FCSTD DOCUMENT  (FreeCAD 0.19R)
Label: fc_assy
License: All rights reserved
LicenseURL: http://en.wikipedia.org/wiki/All_rights_reserved
objects: App::DocumentObjectGroup×2, App::Link×2, PartDesign::CoordinateSystem×1, App::FeaturePython×1, App::Part×1
note: 1 computed .brp shape members not serialized (recipe doc carries the construction recipe); baked Part::Feature solids carry a one-line shape summary decoded from their .brp
EXTERNAL_REF file=fc_box.FCStd obj=LCS_1
EXTERNAL_REF file=fc_box.FCStd obj=Body
EXTERNAL_REF file=cover.FCStd obj=LCS_1
EXTERNAL_REF file=fc_box.FCStd obj=LCS_2
EXTERNAL_REF file=cover.FCStd obj=Body

FEATURE [App::DocumentObjectGroup] Parts
FEATURE [PartDesign::CoordinateSystem] LCS_Origin
  AttacherType = Attacher::AttachEngine3D
  MapMode = 2
  Support = -> [X_Axis]
FEATURE [App::DocumentObjectGroup] Constraints
FEATURE [App::FeaturePython] Variables  # WARN: FeaturePython — macro-defined, semantics opaque (R4)
FEATURE [App::Link] fc_box_Body
  AssemblyType = Asm4EE
  AttachedBy = #LCS_1
  AttachedTo = Parent Assembly#LCS_Origin
  LinkPlacement = pos=(-21,-21,0) rot=(0,0,1;0rad)
  LinkedObject = -> <external fc_box.FCStd>#Body
  Placement = pos=(-21,-21,0) rot=(0,0,1;0rad)
  expr: Placement = LCS_Origin.Placement * AttachmentOffset * fc_box#LCS_1.Placement ^ -1
FEATURE [App::Link] cover_Body
  AssemblyType = Asm4EE
  AttachedBy = #LCS_1
  AttachedTo = fc_box_Body#LCS_2
  AttachmentOffset = pos=(0,0,0) rot=(0,1,0;3.14159rad)
  LinkPlacement = pos=(-21,-92.5,24) rot=(0,0,1;0rad)
  LinkedObject = -> <external cover.FCStd>#Body
  Placement = pos=(-21,-92.5,24) rot=(0,0,1;0rad)
  expr: Placement = fc_box_Body.Placement * fc_box#LCS_2.Placement * AttachmentOffset * cover#LCS_1.Placement ^ -1
FEATURE [App::Part] Model
  Configuration = 0
  Group = -> [LCS_Origin,Constraints,Variables,fc_box_Body,cover_Body]
  Origin = -> Origin
  Type = Assembly4 Model

RESOLVED EXTERNAL PARTS (link-assembly join: the EXTERNAL_REF files above that resolve inside this repo's crawl, each included once):
---- part cover.FCStd = doc fcstd_2b1ffa46e12e ----
FCSTD DOCUMENT  (FreeCAD 0.19R)
Label: cover
License: All rights reserved
LicenseURL: http://en.wikipedia.org/wiki/All_rights_reserved
objects: Sketcher::SketchObject×10, PartDesign::Pad×5, PartDesign::Pocket×5, PartDesign::Chamfer×5, PartDesign::CoordinateSystem×1, PartDesign::Body×1
note: 42 computed .brp shape members not serialized (recipe doc carries the construction recipe); baked Part::Feature solids carry a one-line shape summary decoded from their .brp

FEATURE [Sketcher::SketchObject] Sketch
  FullyConstrained = true
  MapMode = 5
  Support = -> [XY_Plane]
  sketch-geometry (8):
    g0: LineSegment StartX=-23.5 StartY=95 StartZ=0 EndX=23.5 EndY=95 EndZ=0
    g1: LineSegment StartX=23.5 StartY=95 StartZ=0 EndX=23.5 EndY=48 EndZ=0
    g2: LineSegment StartX=23.5 StartY=48 StartZ=0 EndX=20.5 EndY=48 EndZ=0
    g3: LineSegment StartX=20.5 StartY=48 StartZ=0 EndX=20.5 EndY=0 EndZ=0
    g4: LineSegment StartX=20.5 StartY=0 StartZ=0 EndX=-20.5 EndY=0 EndZ=0
    g5: LineSegment StartX=-20.5 StartY=0 StartZ=0 EndX=-20.5 EndY=48 EndZ=0
    g6: LineSegment StartX=-20.5 StartY=48 StartZ=0 EndX=-23.5 EndY=48 EndZ=0
    g7: LineSegment StartX=-23.5 StartY=48 StartZ=0 EndX=-23.5 EndY=95 EndZ=0
  constraints (22):
    c: Coincident(g0,g1)
    c: Vertical(g1)
    c: Coincident(g1,g2)
    c: Horizontal(g2)
    c: Coincident(g2,g3)
    c: Vertical(g3)
    c: Coincident(g3,g4)
    c: Coincident(g4,g5)
    c: Vertical(g5)
    c: Coincident(g5,g6)
    c: Horizontal(g6)
    c: Coincident(g6,g7)
    c: Coincident(g7,g0)
    c: Vertical(g7)
    c: DistanceX(g0,g0) = 47
    c: Symmetric(g0,g0,g-2)
    c: DistanceY(g1,g1) = 47
    c: Equal(g7,g1)
    c: DistanceX(g4,g4) = 41
    c: Symmetric(g4,g3,g-2)
    c: PointOnObject(g3,g-1)
    c: DistanceY(g3,g3) = 48
FEATURE [PartDesign::Pad] Pad
  Direction = (1,1,1)
  Length = 7
  Length2 = 100
  Profile = -> Sketch
  Type = 0
FEATURE [Sketcher::SketchObject] Sketch001
  ExternalGeometry = -> [Pad]
  FullyConstrained = true
  MapMode = 5
  Placement = pos=(0,0,0) rot=(1,0,0;3.14159rad)
  Support = -> [Pad]
  sketch-geometry (8):
    g0: LineSegment StartX=-18.5 StartY=-2 StartZ=0 EndX=18.5 EndY=-2 EndZ=0
    g1: LineSegment StartX=18.5 StartY=-2 StartZ=0 EndX=18.5 EndY=-50 EndZ=0
    g2: LineSegment StartX=18.5 StartY=-50 StartZ=0 EndX=21.5 EndY=-50 EndZ=0
    g3: LineSegment StartX=21.5 StartY=-50 StartZ=0 EndX=21.5 EndY=-93 EndZ=0
    g4: LineSegment StartX=21.5 StartY=-93 StartZ=0 EndX=-21.5 EndY=-93 EndZ=0
    g5: LineSegment StartX=-21.5 StartY=-93 StartZ=0 EndX=-21.5 EndY=-50 EndZ=0
    g6: LineSegment StartX=-21.5 StartY=-50 StartZ=0 EndX=-18.5 EndY=-50 EndZ=0
    g7: LineSegment StartX=-18.5 StartY=-50 StartZ=0 EndX=-18.5 EndY=-2 EndZ=0
  constraints (24):
    c: Horizontal(g0)
    c: Coincident(g0,g1)
    c: Vertical(g1)
    c: Coincident(g1,g2)
    c: Horizontal(g2)
    c: Coincident(g2,g3)
    c: Vertical(g3)
    c: Coincident(g3,g4)
    c: Horizontal(g4)
    c: Coincident(g4,g5)
    c: Vertical(g5)
    c: Coincident(g5,g6)
    c: Horizontal(g6)
    c: Coincident(g6,g7)
    c: Coincident(g7,g0)
    c: Vertical(g7)
    c: DistanceY(g-6,g4) = 2
    c: DistanceX(g-6,g5) = 2
    c: DistanceY(g5,g-6) = 2
    c: DistanceX(g-3,g0) = 2
    c: DistanceX(g0,g-4) = 2
    c: DistanceY(g0,g-3) = 2
    c: DistanceY(g2,g-5) = 2
    c: DistanceX(g3,g-5) = 2
FEATURE [PartDesign::Pocket] Pocket
  BaseFeature = -> Pad
  Length = 5
  Length2 = 100
  Profile = -> Sketch001
  Type = 0
FEATURE [PartDesign::CoordinateSystem] LCS_1
  AttacherType = Attacher::AttachEngine3D
  AttachmentOffset = pos=(0,0,-21.5) rot=(0,0,1;0rad)
  MapMode = 7
  Placement = pos=(0,93,5) rot=(0.57735,0.57735,0.57735;2.0944rad)
  Support = -> [Pocket]
FEATURE [Sketcher::SketchObject] Sketch002
  ExternalGeometry = -> [Pocket]
  FullyConstrained = true
  MapMode = 5
  Placement = pos=(0,0,7) rot=(0,0,1;0rad)
  Support = -> [Pocket]
  sketch-geometry (8):
    g0: LineSegment StartX=-16 StartY=46 StartZ=0 EndX=16 EndY=46 EndZ=0
    g1: LineSegment StartX=16 StartY=46 StartZ=0 EndX=16 EndY=43 EndZ=0
    g2: LineSegment StartX=16 StartY=43 StartZ=0 EndX=-16 EndY=43 EndZ=0
    g3: LineSegment StartX=-16 StartY=43 StartZ=0 EndX=-16 EndY=46 EndZ=0
    g4: LineSegment StartX=-16 StartY=37 StartZ=0 EndX=16 EndY=37 EndZ=0
    g5: LineSegment StartX=16 StartY=37 StartZ=0 EndX=16 EndY=34 EndZ=0
    g6: LineSegment StartX=16 StartY=34 StartZ=0 EndX=-16 EndY=34 EndZ=0
    g7: LineSegment StartX=-16 StartY=34 StartZ=0 EndX=-16 EndY=37 EndZ=0
  constraints (22):
    c: Coincident(g0,g1)
    c: Coincident(g1,g2)
    c: Coincident(g2,g3)
    c: Coincident(g3,g0)
    c: Horizontal(g0)
    c: Vertical(g1)
    c: Vertical(g3)
    c: Coincident(g4,g5)
    c: Coincident(g5,g6)
    c: Coincident(g6,g7)
    c: Coincident(g7,g4)
    c: Horizontal(g6)
    c: Vertical(g5)
    c: Vertical(g7)
    c: Equal(g5,g1)
    c: Symmetric(g1,g2,g-2)
    c: DistanceY(g1,g-3) = 5
    c: Equal(g4,g2)
    c: Symmetric(g4,g4,g-2)
    c: DistanceY(g4,g1) = 6
    c: DistanceY(g5,g4) = 3
    c: DistanceX(g4,g4) = 32
FEATURE [PartDesign::Pad] Pad001
  BaseFeature = -> Pocket
  Direction = (1,1,1)
  Length = 5
  Length2 = 100
  Profile = -> Sketch002
  Type = 0
FEATURE [Sketcher::SketchObject] Sketch003
  ExternalGeometry = -> [Pad001]
  FullyConstrained = true
  MapMode = 5
  Placement = pos=(0,0,7) rot=(0,0,1;0rad)
  Support = -> [Pad001]
  sketch-geometry (4):
    g0: LineSegment StartX=-20.5 StartY=87 StartZ=0 EndX=-10.5 EndY=87 EndZ=0
    g1: LineSegment StartX=-10.5 StartY=87 StartZ=0 EndX=-10.5 EndY=75 EndZ=0
    g2: LineSegment StartX=-10.5 StartY=75 StartZ=0 EndX=-20.5 EndY=75 EndZ=0
    g3: LineSegment StartX=-20.5 StartY=75 StartZ=0 EndX=-20.5 EndY=87 EndZ=0
  constraints (12):
    c: Coincident(g0,g1)
    c: Coincident(g1,g2)
    c: Coincident(g2,g3)
    c: Coincident(g3,g0)
    c: Horizontal(g0)
    c: Horizontal(g2)
    c: Vertical(g1)
    c: Vertical(g3)
    c: DistanceX(g0,g0) = 10
    c: DistanceY(g1,g1) = 12
    c: DistanceY(g0,g-3) = 8
    c: DistanceX(g-3,g0) = 3
FEATURE [PartDesign::Pocket] Pocket001
  BaseFeature = -> Pad001
  Length = 2
  Length2 = 100
  Profile = -> Sketch003
  Type = 0
FEATURE [Sketcher::SketchObject] Sketch004
  ExternalGeometry = -> [Pocket001]
  FullyConstrained = true
  MapMode = 5
  Placement = pos=(0,0,7) rot=(0,0,1;0rad)
  Support = -> [Pocket001]
  sketch-geometry (8):
    g0: LineSegment StartX=-9.5 StartY=95 StartZ=0 EndX=15.5 EndY=95 EndZ=0
    g1: LineSegment StartX=-9.5 StartY=95 StartZ=0 EndX=-9.5 EndY=73 EndZ=0
    g2: LineSegment StartX=15.5 StartY=73 StartZ=0 EndX=15.5 EndY=95 EndZ=0
    g3: LineSegment StartX=-9.5 StartY=73 StartZ=0 EndX=-7.5 EndY=73 EndZ=0
    g4: LineSegment StartX=15.5 StartY=73 StartZ=0 EndX=13.5 EndY=73 EndZ=0
    g5: LineSegment StartX=-7.5 StartY=73 StartZ=0 EndX=-7.5 EndY=88 EndZ=0
    g6: LineSegment StartX=-7.5 StartY=88 StartZ=0 EndX=13.5 EndY=88 EndZ=0
    g7: LineSegment StartX=13.5 StartY=88 StartZ=0 EndX=13.5 EndY=73 EndZ=0
  constraints (24):
    c: PointOnObject(g0,g-3)
    c: PointOnObject(g0,g-3)
    c: DistanceX(g0,g0) = 25
    c: DistanceX(g-3,g0) = 14
    c: Coincident(g0,g1)
    c: Vertical(g1)
    c: Coincident(g2,g0)
    c: Vertical(g2)
    c: Coincident(g3,g1)
    c: Horizontal(g3)
    c: Coincident(g4,g2)
    c: Horizontal(g4)
    c: Equal(g4,g3)
    c: DistanceX(g4,g4) = 2
    c: Equal(g2,g1)
    c: DistanceY(g2,g2) = 22
    c: Coincident(g3,g5)
    c: Vertical(g5)
    c: Coincident(g5,g6)
    c: Horizontal(g6)
    c: Coincident(g6,g7)
    c: Coincident(g7,g4)
    c: Vertical(g7)
    c: DistanceY(g6,g0) = 7
FEATURE [PartDesign::Pad] Pad002
  BaseFeature = -> Pocket001
  Direction = (1,1,1)
  Length = 20
  Length2 = 100
  Profile = -> Sketch004
  Type = 0
FEATURE [Sketcher::SketchObject] Sketch005
  ExternalGeometry = -> [Pad002]
  FullyConstrained = true
  MapMode = 5
  Placement = pos=(-7.5,0,0) rot=(0.57735,0.57735,0.57735;2.0944rad)
  Support = -> [Pad002]
  sketch-geometry (2):
    g0: ArcOfCircle CenterX=81 CenterY=7 CenterZ=0 NormalX=0 NormalY=0 NormalZ=1 AngleXU=0 Radius=6 StartAngle=1.42e-14 EndAngle=3.14159
    g1: LineSegment StartX=75 StartY=7 StartZ=0 EndX=87 EndY=7 EndZ=0
  constraints (5):
    c: PointOnObject(g0,g-3)
    c: Coincident(g0,g-4)
    c: Coincident(g0,g-5)
    c: Coincident(g1,g0)
    c: Coincident(g1,g0)
FEATURE [PartDesign::Pocket] Pocket002
  BaseFeature = -> Pad002
  Length = 5
  Length2 = 100
  Profile = -> Sketch005
  Type = 0
FEATURE [Sketcher::SketchObject] Sketch006
  ExternalGeometry = -> [Pad002]
  FullyConstrained = true
  MapMode = 5
  Placement = pos=(-5.42e-14,95,0) rot=(0,0.707107,0.707107;3.14159rad)
  Support = -> [Pad002]
  sketch-geometry (1):
    g0: Circle CenterX=-3 CenterY=18 CenterZ=0 NormalX=0 NormalY=0 NormalZ=1 AngleXU=0 Radius=5
  constraints (3):
    c: Diameter(g0) = 10
    c: DistanceY(g0,g-3) = 9
    c: DistanceX(g-3,g0) = 12.5
FEATURE [PartDesign::Pocket] Pocket003
  BaseFeature = -> Pocket002
  Length = 7
  Length2 = 100
  Profile = -> Sketch006
  Type = 0
FEATURE [Sketcher::SketchObject] Sketch007
  ExternalGeometry = -> [Pocket003]
  FullyConstrained = true
  MapMode = 5
  Placement = pos=(0,0,27) rot=(0,0,1;0rad)
  Support = -> [Pocket003]
  sketch-geometry (8):
    g0: LineSegment StartX=-9.5 StartY=73 StartZ=0 EndX=-0.5 EndY=73 EndZ=0
    g1: LineSegment StartX=-0.5 StartY=73 StartZ=0 EndX=-0.5 EndY=81 EndZ=0
    g2: LineSegment StartX=-0.5 StartY=81 StartZ=0 EndX=6.5 EndY=81 EndZ=0
    g3: LineSegment StartX=6.5 StartY=81 StartZ=0 EndX=6.5 EndY=73 EndZ=0
    g4: LineSegment StartX=6.5 StartY=73 StartZ=0 EndX=15.5 EndY=73 EndZ=0
    g5: LineSegment StartX=15.5 StartY=73 StartZ=0 EndX=15.5 EndY=95 EndZ=0
    g6: LineSegment StartX=15.5 StartY=95 StartZ=0 EndX=-9.5 EndY=95 EndZ=0
    g7: LineSegment StartX=-9.5 StartY=95 StartZ=0 EndX=-9.5 EndY=73 EndZ=0
  constraints (20):
    c: Coincident(g-3,g0)
    c: Horizontal(g0)
    c: Coincident(g0,g1)
    c: Vertical(g1)
    c: Coincident(g1,g2)
    c: Horizontal(g2)
    c: Coincident(g2,g3)
    c: Vertical(g3)
    c: Coincident(g3,g4)
    c: Coincident(g4,g-5)
    c: Coincident(g4,g5)
    c: Coincident(g5,g-5)
    c: Coincident(g5,g6)
    c: Coincident(g6,g-4)
    c: Coincident(g6,g7)
    c: Coincident(g7,g0)
    c: Horizontal(g4)
    c: Equal(g0,g4)
    c: DistanceY(g2,g-6) = 7
    c: DistanceX(g2,g2) = 7
FEATURE [PartDesign::Pad] Pad003
  BaseFeature = -> Pocket003
  Direction = (1,1,1)
  Length = 3
  Length2 = 100
  Profile = -> Sketch007
  Type = 0
FEATURE [Sketcher::SketchObject] Sketch008
  ExternalGeometry = -> [Pad003]
  FullyConstrained = true
  MapMode = 5
  Placement = pos=(0,0,30) rot=(0,0,1;0rad)
  Support = -> [Pad003]
  sketch-geometry (9):
    g0: LineSegment StartX=-0.5 StartY=73 StartZ=0 EndX=-0.5 EndY=81 EndZ=0
    g1: LineSegment StartX=-0.5 StartY=81 StartZ=0 EndX=6.5 EndY=81 EndZ=0
    g2: LineSegment StartX=6.5 StartY=81 StartZ=0 EndX=6.5 EndY=73 EndZ=0
    g3: LineSegment StartX=6.5 StartY=73 StartZ=0 EndX=9.5 EndY=73 EndZ=0
    g4: LineSegment StartX=9.5 StartY=73 StartZ=0 EndX=9.5 EndY=82 EndZ=0
    g5: LineSegment StartX=9.5 StartY=82 StartZ=0 EndX=2.5 EndY=95 EndZ=0
    g6: LineSegment StartX=2.5 StartY=95 StartZ=0 EndX=-3.5 EndY=82 EndZ=0
    g7: LineSegment StartX=-3.5 StartY=82 StartZ=0 EndX=-3.5 EndY=73 EndZ=0
    g8: LineSegment StartX=-3.5 StartY=73 StartZ=0 EndX=-0.5 EndY=73 EndZ=0
  constraints (23):
    c: Coincident(g-6,g0)
    c: Coincident(g0,g-6)
    c: Coincident(g0,g1)
    c: Coincident(g1,g-5)
    c: Coincident(g1,g2)
    c: Coincident(g2,g-5)
    c: Coincident(g2,g3)
    c: Horizontal(g3)
    c: Coincident(g3,g4)
    c: Vertical(g4)
    c: Coincident(g4,g5)
    c: PointOnObject(g5,g-3)
    c: Coincident(g5,g6)
    c: Coincident(g6,g7)
    c: Vertical(g7)
    c: Coincident(g7,g8)
    c: Coincident(g8,g0)
    c: Horizontal(g8)
    c: Equal(g7,g4)
    c: Equal(g8,g3)
    c: DistanceX(g3,g3) = 3
    c: DistanceY(g7,g7) = 9
    c: DistanceX(g5,g4) = 7
FEATURE [PartDesign::Pad] Pad004
  BaseFeature = -> Pad003
  Direction = (1,1,1)
  Length = 40
  Length2 = 100
  Profile = -> Sketch008
  Type = 0
FEATURE [PartDesign::Chamfer] Chamfer
  Angle = 45
  Base = -> Pad004 [Edge58]
  BaseFeature = -> Pad004
  ChamferType = 0
  FlipDirection = false
  Size = 5
  Size2 = 1
  SupportTransform = false
FEATURE [PartDesign::Chamfer] Chamfer001
  Angle = 45
  Base = -> Chamfer [Edge46]
  BaseFeature = -> Chamfer
  ChamferType = 0
  FlipDirection = false
  Size = 5
  Size2 = 1
  SupportTransform = false
FEATURE [PartDesign::Chamfer] Chamfer002
  Angle = 45
  Base = -> Chamfer001 [Edge176,Edge174]
  BaseFeature = -> Chamfer001
  ChamferType = 0
  FlipDirection = false
  Size = 3
  Size2 = 1
  SupportTransform = false
FEATURE [PartDesign::Chamfer] Chamfer003
  Angle = 45
  Base = -> Chamfer002 [Edge156]
  BaseFeature = -> Chamfer002
  ChamferType = 0
  FlipDirection = false
  Size = 1
  Size2 = 1
  SupportTransform = false
FEATURE [PartDesign::Chamfer] Chamfer004
  Angle = 45
  Base = -> Chamfer003 [Edge106]
  BaseFeature = -> Chamfer003
  ChamferType = 0
  FlipDirection = false
  Size = 1
  Size2 = 1
  SupportTransform = false
FEATURE [Sketcher::SketchObject] Sketch009
  ExternalGeometry = -> [Chamfer004]
  FullyConstrained = true
  MapMode = 5
  Placement = pos=(15.5,0,0) rot=(0.57735,0.57735,0.57735;2.0944rad)
  Support = -> [Chamfer004]
  sketch-geometry (1):
    g0: Circle CenterX=78 CenterY=19 CenterZ=0 NormalX=0 NormalY=0 NormalZ=1 AngleXU=0 Radius=2.5
  constraints (3):
    c: Diameter(g0) = 5
    c: DistanceX(g-3,g0) = 5
    c: DistanceY(g0,g-3) = 8
FEATURE [PartDesign::Pocket] Pocket004
  BaseFeature = -> Chamfer004
  Length = 5
  Length2 = 100
  Profile = -> Sketch009
  Type = 1
FEATURE [PartDesign::Body] Body
  Group = -> [Sketch,Pad,Sketch001,Pocket,LCS_1,Sketch002,Pad001,Sketch003,Pocket001,Sketch004,Pad002,Sketch005,Pocket002,Sketch006,Pocket003,Sketch007,Pad003,Sketch008,Pad004,Chamfer,Chamfer001,Chamfer002,Chamfer003,Chamfer004,Sketch009,Pocket004]
  Origin = -> Origin
  Tip = -> Pocket004
---- part fc_box.FCStd = doc fcstd_bd3612893a7e ----
FCSTD DOCUMENT  (FreeCAD 0.19R)
Label: fc_box
License: All rights reserved
LicenseURL: http://en.wikipedia.org/wiki/All_rights_reserved
objects: Sketcher::SketchObject×9, PartDesign::Pocket×5, PartDesign::Pad×4, PartDesign::CoordinateSystem×2, PartDesign::Body×1
note: 30 computed .brp shape members not serialized (recipe doc carries the construction recipe); baked Part::Feature solids carry a one-line shape summary decoded from their .brp

FEATURE [Sketcher::SketchObject] Sketch
  FullyConstrained = true
  MapMode = 5
  Support = -> [XY_Plane]
  sketch-geometry (12):
    g0: LineSegment StartX=-21 StartY=21 StartZ=0 EndX=21 EndY=21 EndZ=0
    g1: LineSegment StartX=21 StartY=21 StartZ=0 EndX=21 EndY=-21 EndZ=0
    g2: LineSegment StartX=-21 StartY=-21 StartZ=0 EndX=-21 EndY=21 EndZ=0
    g3: Circle CenterX=-15 CenterY=15 CenterZ=0 NormalX=0 NormalY=0 NormalZ=1 AngleXU=0 Radius=1.75
    g4: Circle CenterX=15 CenterY=15 CenterZ=0 NormalX=0 NormalY=0 NormalZ=1 AngleXU=0 Radius=1.75
    g5: Circle CenterX=-15 CenterY=-15 CenterZ=0 NormalX=0 NormalY=0 NormalZ=1 AngleXU=0 Radius=1.75
    g6: Circle CenterX=15 CenterY=-15 CenterZ=0 NormalX=0 NormalY=0 NormalZ=1 AngleXU=0 Radius=1.75
    g7: LineSegment StartX=-18 StartY=-69 StartZ=0 EndX=18 EndY=-69 EndZ=0
    g8: LineSegment StartX=-21 StartY=-21 StartZ=0 EndX=-18 EndY=-21 EndZ=0
    g9: LineSegment StartX=21 StartY=-21 StartZ=0 EndX=18 EndY=-21 EndZ=0
    g10: LineSegment StartX=-18 StartY=-69 StartZ=0 EndX=-18 EndY=-21 EndZ=0
    g11: LineSegment StartX=18 StartY=-69 StartZ=0 EndX=18 EndY=-21 EndZ=0
  constraints (31):
    c: Coincident(g0,g1)
    c: Coincident(g2,g0)
    c: Vertical(g2)
    c: Symmetric(g0,g0,g-2)
    c: Symmetric(g1,g0,g-1)
    c: DistanceX(g0,g0) = 42
    c: Equal(g3,g4)
    c: Equal(g4,g6)
    c: Equal(g6,g5)
    c: Diameter(g3) = 3.5
    c: DistanceX(g0,g3) = 6
    c: Symmetric(g3,g4,g-2)
    c: DistanceY(g3,g0) = 6
    c: Symmetric(g5,g6,g-2)
    c: DistanceX(g0,g5) = 6
    c: DistanceY(g5,g3) = 30
    c: DistanceY(g1,g1) = 42
    c: Equal(g2,g1)
    c: Symmetric(g7,g7,g-2)
    c: Coincident(g8,g2)
    c: Horizontal(g8)
    c: Coincident(g9,g1)
    c: Horizontal(g9)
    c: Equal(g8,g9)
    c: Coincident(g10,g7)
    c: Coincident(g10,g8)
    c: Vertical(g10)
    c: Coincident(g11,g7)
    c: Coincident(g11,g9)
    c: DistanceX(g7,g7) = 36
    c: DistanceY(g11,g11) = 48
FEATURE [PartDesign::Pad] Pad
  Direction = (1,1,1)
  Length = 4
  Length2 = 100
  Profile = -> Sketch
  Type = 0
FEATURE [Sketcher::SketchObject] Sketch001
  ExternalGeometry = -> [Pad]
  FullyConstrained = true
  MapMode = 5
  Placement = pos=(0,0,4) rot=(0,0,1;0rad)
  Support = -> [Pad]
  sketch-geometry (16):
    g0: LineSegment StartX=-19 StartY=19 StartZ=0 EndX=-19 EndY=-19 EndZ=0
    g1: LineSegment StartX=-19 StartY=-19 StartZ=0 EndX=-16 EndY=-19 EndZ=0
    g2: LineSegment StartX=-16 StartY=-19 StartZ=0 EndX=-16 EndY=-67 EndZ=0
    g3: LineSegment StartX=-16 StartY=-67 StartZ=0 EndX=16 EndY=-67 EndZ=0
    g4: LineSegment StartX=16 StartY=-67 StartZ=0 EndX=16 EndY=-19 EndZ=0
    g5: LineSegment StartX=16 StartY=-19 StartZ=0 EndX=19 EndY=-19 EndZ=0
    g6: LineSegment StartX=19 StartY=-19 StartZ=0 EndX=19 EndY=19 EndZ=0
    g7: LineSegment StartX=19 StartY=19 StartZ=0 EndX=-19 EndY=19 EndZ=0
    g8: LineSegment StartX=-21 StartY=21 StartZ=0 EndX=21 EndY=21 EndZ=0
    g9: LineSegment StartX=21 StartY=21 StartZ=0 EndX=21 EndY=-21 EndZ=0
    g10: LineSegment StartX=21 StartY=-21 StartZ=0 EndX=18 EndY=-21 EndZ=0
    g11: LineSegment StartX=18 StartY=-21 StartZ=0 EndX=18 EndY=-69 EndZ=0
    g12: LineSegment StartX=18 StartY=-69 StartZ=0 EndX=-18 EndY=-69 EndZ=0
    g13: LineSegment StartX=-18 StartY=-69 StartZ=0 EndX=-18 EndY=-21 EndZ=0
    g14: LineSegment StartX=-18 StartY=-21 StartZ=0 EndX=-21 EndY=-21 EndZ=0
    g15: LineSegment StartX=-21 StartY=-21 StartZ=0 EndX=-21 EndY=21 EndZ=0
  constraints (40):
    c: Vertical(g0)
    c: Coincident(g0,g1)
    c: Coincident(g1,g2)
    c: Vertical(g2)
    c: Coincident(g2,g3)
    c: Horizontal(g3)
    c: Coincident(g3,g4)
    c: Vertical(g4)
    c: Coincident(g4,g5)
    c: Coincident(g5,g6)
    c: Vertical(g6)
    c: Coincident(g6,g7)
    c: Coincident(g7,g0)
    c: Horizontal(g7)
    c: Horizontal(g5)
    c: Horizontal(g1)
    c: Coincident(g-3,g8)
    c: Coincident(g8,g-4)
    c: Coincident(g8,g9)
    c: Coincident(g9,g-4)
    c: Coincident(g9,g10)
    c: Coincident(g10,g-5)
    c: Coincident(g10,g11)
    c: Coincident(g11,g-5)
    c: Coincident(g11,g12)
    c: Coincident(g12,g-6)
    c: Coincident(g12,g13)
    c: Coincident(g13,g-6)
    c: Coincident(g13,g14)
    c: Coincident(g14,g-3)
    c: Coincident(g14,g15)
    c: Coincident(g15,g8)
    c: DistanceX(g8,g0) = 2
    c: DistanceY(g0,g8) = 2
    c: DistanceX(g6,g8) = 2
    c: DistanceY(g9,g5) = 2
    c: DistanceX(g4,g10) = 2
    c: DistanceY(g11,g3) = 2
    c: DistanceX(g12,g2) = 2
    c: DistanceY(g14,g0) = 2
FEATURE [PartDesign::Pad] Pad001
  BaseFeature = -> Pad
  Direction = (1,1,1)
  Length = 25
  Length2 = 100
  Profile = -> Sketch001
  Type = 0
FEATURE [Sketcher::SketchObject] Sketch002
  ExternalGeometry = -> [Pad001]
  FullyConstrained = true
  MapMode = 5
  Placement = pos=(0,-69,0) rot=(1,0,0;1.5708rad)
  Support = -> [Pad001]
  sketch-geometry (4):
    g0: LineSegment StartX=-8 StartY=4 StartZ=0 EndX=8 EndY=4 EndZ=0
    g1: LineSegment StartX=8 StartY=4 StartZ=0 EndX=8 EndY=14 EndZ=0
    g2: LineSegment StartX=8 StartY=14 StartZ=0 EndX=-8 EndY=14 EndZ=0
    g3: LineSegment StartX=-8 StartY=14 StartZ=0 EndX=-8 EndY=4 EndZ=0
  constraints (11):
    c: Coincident(g0,g1)
    c: Coincident(g1,g2)
    c: Coincident(g2,g3)
    c: Coincident(g3,g0)
    c: Horizontal(g2)
    c: Vertical(g1)
    c: Vertical(g3)
    c: PointOnObject(g0,g-3)
    c: DistanceY(g1,g1) = 10
    c: DistanceX(g2,g2) = 16
    c: Symmetric(g0,g0,g-2)
FEATURE [PartDesign::Pocket] Pocket
  BaseFeature = -> Pad001
  Length = 2
  Length2 = 100
  Profile = -> Sketch002
  Type = 0
FEATURE [Sketcher::SketchObject] Sketch003
  ExternalGeometry = -> [Pocket]
  FullyConstrained = true
  MapMode = 5
  Placement = pos=(21,0,0) rot=(0.57735,0.57735,0.57735;2.0944rad)
  Support = -> [Pocket]
  sketch-geometry (4):
    g0: LineSegment StartX=-1 StartY=22 StartZ=0 EndX=15 EndY=22 EndZ=0
    g1: LineSegment StartX=15 StartY=22 StartZ=0 EndX=15 EndY=6 EndZ=0
    g2: LineSegment StartX=15 StartY=6 StartZ=0 EndX=-1 EndY=6 EndZ=0
    g3: LineSegment StartX=-1 StartY=6 StartZ=0 EndX=-1 EndY=22 EndZ=0
  constraints (12):
    c: Coincident(g0,g1)
    c: Coincident(g1,g2)
    c: Coincident(g2,g3)
    c: Coincident(g3,g0)
    c: Horizontal(g0)
    c: Horizontal(g2)
    c: Vertical(g1)
    c: Vertical(g3)
    c: DistanceY(g1,g1) = 16
    c: DistanceX(g0,g0) = 16
    c: DistanceY(g-3,g1) = 2
    c: DistanceX(g1,g-3) = 6
FEATURE [PartDesign::Pocket] Pocket001
  BaseFeature = -> Pocket
  Length = 2
  Length2 = 100
  Profile = -> Sketch003
  Type = 0
FEATURE [PartDesign::CoordinateSystem] LCS_1
  AttacherType = Attacher::AttachEngine3D
  MapMode = 1
  Placement = pos=(21,21,0) rot=(0,0,1;0rad)
  Support = -> [Pocket001]
FEATURE [PartDesign::CoordinateSystem] LCS_2
  AttacherType = Attacher::AttachEngine3D
  AttachmentOffset = pos=(-0.5,0,-21) rot=(0,0,1;0rad)
  MapMode = 7
  Placement = pos=(0,21.5,29) rot=(0.57735,-0.57735,-0.57735;2.0944rad)
  Support = -> [Pocket001]
FEATURE [Sketcher::SketchObject] Sketch004
  ExternalGeometry = -> [Pocket001]
  FullyConstrained = true
  MapMode = 5
  Placement = pos=(18,2.54023e-11,0) rot=(0.57735,0.57735,0.57735;2.0944rad)
  Support = -> [Pocket001]
  sketch-geometry (4):
    g0: LineSegment StartX=-37 StartY=16 StartZ=0 EndX=-25 EndY=16 EndZ=0
    g1: LineSegment StartX=-25 StartY=16 StartZ=0 EndX=-25 EndY=8 EndZ=0
    g2: LineSegment StartX=-25 StartY=8 StartZ=0 EndX=-37 EndY=8 EndZ=0
    g3: LineSegment StartX=-37 StartY=8 StartZ=0 EndX=-37 EndY=16 EndZ=0
  constraints (12):
    c: Coincident(g0,g1)
    c: Coincident(g1,g2)
    c: Coincident(g2,g3)
    c: Coincident(g3,g0)
    c: Horizontal(g0)
    c: Horizontal(g2)
    c: Vertical(g1)
    c: Vertical(g3)
    c: DistanceY(g1,g1) = 8
    c: DistanceX(g0,g0) = 12
    c: DistanceX(g1,g-3) = 4
    c: DistanceY(g-3,g1) = 4
FEATURE [PartDesign::Pad] Pad002
  BaseFeature = -> Pocket001
  Direction = (1,1,1)
  Length = 8
  Length2 = 100
  Profile = -> Sketch004
  Type = 0
FEATURE [Sketcher::SketchObject] Sketch005
  ExternalGeometry = -> [Pad002]
  FullyConstrained = true
  MapMode = 5
  Placement = pos=(-18,0,0) rot=(0.57735,-0.57735,-0.57735;2.0944rad)
  Support = -> [Pad002]
  sketch-geometry (4):
    g0: LineSegment StartX=25 StartY=16 StartZ=0 EndX=37 EndY=16 EndZ=0
    g1: LineSegment StartX=37 StartY=16 StartZ=0 EndX=37 EndY=8 EndZ=0
    g2: LineSegment StartX=37 StartY=8 StartZ=0 EndX=25 EndY=8 EndZ=0
    g3: LineSegment StartX=25 StartY=8 StartZ=0 EndX=25 EndY=16 EndZ=0
  constraints (12):
    c: Coincident(g0,g1)
    c: Coincident(g1,g2)
    c: Coincident(g2,g3)
    c: Coincident(g3,g0)
    c: Horizontal(g0)
    c: Horizontal(g2)
    c: Vertical(g1)
    c: Vertical(g3)
    c: DistanceY(g1,g1) = 8
    c: DistanceX(g0,g0) = 12
    c: DistanceX(g-3,g2) = 4
    c: DistanceY(g-3,g2) = 4
FEATURE [PartDesign::Pad] Pad003
  BaseFeature = -> Pad002
  Direction = (1,1,1)
  Length = 8
  Length2 = 100
  Profile = -> Sketch005
  Type = 0
FEATURE [Sketcher::SketchObject] Sketch006
  ExternalGeometry = -> [Pad003]
  FullyConstrained = true
  MapMode = 5
  Placement = pos=(0,0,16) rot=(0,0,1;0rad)
  Support = -> [Pad003]
  sketch-geometry (8):
    g0: LineSegment StartX=-23 StartY=-28 StartZ=0 EndX=-18 EndY=-28 EndZ=0
    g1: LineSegment StartX=-18 StartY=-28 StartZ=0 EndX=-18 EndY=-34 EndZ=0
    g2: LineSegment StartX=-18 StartY=-34 StartZ=0 EndX=-23 EndY=-34 EndZ=0
    g3: LineSegment StartX=-23 StartY=-34 StartZ=0 EndX=-23 EndY=-28 EndZ=0
    g4: LineSegment StartX=18 StartY=-28 StartZ=0 EndX=23 EndY=-28 EndZ=0
    g5: LineSegment StartX=23 StartY=-28 StartZ=0 EndX=23 EndY=-34 EndZ=0
    g6: LineSegment StartX=23 StartY=-34 StartZ=0 EndX=18 EndY=-34 EndZ=0
    g7: LineSegment StartX=18 StartY=-34 StartZ=0 EndX=18 EndY=-28 EndZ=0
  constraints (23):
    c: Coincident(g0,g1)
    c: Coincident(g1,g2)
    c: Coincident(g2,g3)
    c: Coincident(g3,g0)
    c: Horizontal(g0)
    c: Horizontal(g2)
    c: Vertical(g1)
    c: Vertical(g3)
    c: Coincident(g4,g5)
    c: Coincident(g5,g6)
    c: Coincident(g6,g7)
    c: Coincident(g7,g4)
    c: Horizontal(g4)
    c: Horizontal(g6)
    c: Vertical(g5)
    c: Vertical(g7)
    c: Equal(g7,g1)
    c: Equal(g4,g0)
    c: Symmetric(g6,g1,g-2)
    c: DistanceY(g5,g5) = 6
    c: DistanceY(g-4,g5) = 3
    c: DistanceX(g6,g6) = 5
    c: DistanceX(g0,g4) = 36
FEATURE [PartDesign::Pocket] Pocket002
  BaseFeature = -> Pad003
  Length = 8
  Length2 = 100
  Profile = -> Sketch006
  Type = 0
FEATURE [Sketcher::SketchObject] Sketch007
  ExternalGeometry = -> [Pocket002]
  FullyConstrained = true
  MapMode = 5
  Placement = pos=(18,2.54023e-11,0) rot=(0.57735,0.57735,0.57735;2.0944rad)
  Support = -> [Pocket002]
  sketch-geometry (1):
    g0: Circle CenterX=-47 CenterY=16 CenterZ=0 NormalX=0 NormalY=0 NormalZ=1 AngleXU=0 Radius=5
  constraints (3):
    c: Diameter(g0) = 10
    c: DistanceY(g-3,g0) = 12
    c: DistanceX(g-3,g0) = 22
FEATURE [PartDesign::Pocket] Pocket003
  BaseFeature = -> Pocket002
  Length = 5
  Length2 = 100
  Profile = -> Sketch007
  Type = 1
FEATURE [Sketcher::SketchObject] Sketch008
  ExternalGeometry = -> [Pocket003]
  FullyConstrained = true
  MapMode = 5
  Placement = pos=(0,0,0) rot=(1,0,0;3.14159rad)
  Support = -> [Pocket003]
  sketch-geometry (4):
    g0: Circle CenterX=-15 CenterY=-15 CenterZ=0 NormalX=0 NormalY=0 NormalZ=1 AngleXU=0 Radius=4
    g1: Circle CenterX=-15 CenterY=15 CenterZ=0 NormalX=0 NormalY=0 NormalZ=1 AngleXU=0 Radius=4
    g2: Circle CenterX=15 CenterY=15 CenterZ=0 NormalX=0 NormalY=0 NormalZ=1 AngleXU=0 Radius=4
    g3: Circle CenterX=15 CenterY=-15 CenterZ=0 NormalX=0 NormalY=0 NormalZ=1 AngleXU=0 Radius=4
  constraints (8):
    c: Coincident(g0,g-6)
    c: Coincident(g1,g-3)
    c: Coincident(g2,g-4)
    c: Coincident(g3,g-5)
    c: Equal(g0,g1)
    c: Equal(g1,g2)
    c: Equal(g2,g3)
    c: Diameter(g2) = 8
FEATURE [PartDesign::Pocket] Pocket004
  BaseFeature = -> Pocket003
  Length = 2
  Length2 = 100
  Profile = -> Sketch008
  Type = 0
FEATURE [PartDesign::Body] Body
  Group = -> [Sketch,Pad,Sketch001,Pad001,Sketch002,Pocket,Sketch003,Pocket001,LCS_1,LCS_2,Sketch004,Pad002,Sketch005,Pad003,Sketch006,Pocket002,Sketch007,Pocket003,Sketch008,Pocket004]
  Origin = -> Origin
  Tip = -> Pocket004
